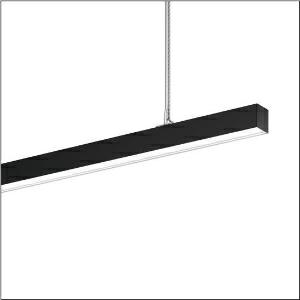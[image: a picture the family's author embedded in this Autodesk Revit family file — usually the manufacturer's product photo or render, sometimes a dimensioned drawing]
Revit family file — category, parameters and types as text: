
# Revit family: silica_r__21_51mx33dc3dbb_6d07
name_source: partatom
category: Lighting Fixtures
units: mm (PartAtom-declared; Revit-internal decimal feet)

## family parameters
Cut with Voids When Loaded = No
Host = Face
Light Source = No
Part Type = Normal
Room Calculation Point = No
Round Connector Dimension = Use Diameter
Shared = No

## types (1)
- --- (1 x LED, 14780 lm, 99.5 W, 3000K)
    Apparent Load = 100 VA
    CIE Flux Codes = 78 96 99 55 100
    Color Rendering = 80
    Color Temperature = 3000K
    Default Elevation = 1800 mm
    Description = Silica® 21, office luminaire, primary optical cover: prismatic diffuser, of PMMA, CAT 2 (L<= 3000cd/m²), light emission: direct/indirect distribution, primary light characteristic: symmetric, installation type: suspended mounting, LED, rated luminous flux: 14.780lm, luminous efficacy: 149lm/W, light colour: 830, colour temperature: 3000K, with terminal, 3+2-pole, max. 2.5mm², mains connection: 220..240V, AC, 50/60Hz, rated input power: 99.5W, luminaire housing, of aluminium, jet black (RAL 9005), length: 3.004mm, width: 53mm, height: 53mm, protection rating (complete): IP20, insulation class (complete): insulation class I (protective earthing), certification: CE, permissible operating ambient temperature: 0..+35°C, standard: EN 50419, packaging unit: 1 piece
    Height = 53 mm
    Lamp = 1 x LED
    Lamp Light Flux = 14780 lm
    Lamp Power = 99.5 W
    Lamp count = 1
    Length = 3004 mm
    Luminous efficacy = 149 lm/W
    Manufacturer = Siteco
    ModVariant = No
    Model = 51MX33DC3DBB
    Mounting Place = Ceiling
    Mounting Type = Pendant
    Number of Poles = 1
    OnlyDefault = Yes
    Power Factor = 1
    Product Name = Silica® 21
    Product group = office luminaire | ceiling pendant
    ProductGroupID = 902
    Protection Class = Protection class I
    Protection Degree = IP 20
    RLX_Detail_Level = 1
    RLX_Emergency_Light_Flux = 0 lm
    RLX_Emergency_Type = 0
    RLX_Emergency_Type_DB = No
    RlxData = <blob elided: 26101 chars, md5=b03a57e6>
    Socket = socket
    Standby Power = 0 W
    System Light Flux = 14780 lm
    System Power = 100 W
    Type Comments = factory setting: luminous flux: 100 % | dim-lin: 254 | 345 mA
    Type Image = l_1335856.jpg
    URL = http://relux.com
    VarID = @adj_087795
    Voltage = 0 V
    Weight = 0.00 kg
    Width = 53 mm

## geometry (parser evidence)
native form markers: Blend x4, Sweep x14
no freeform markers — native parametric forms only
